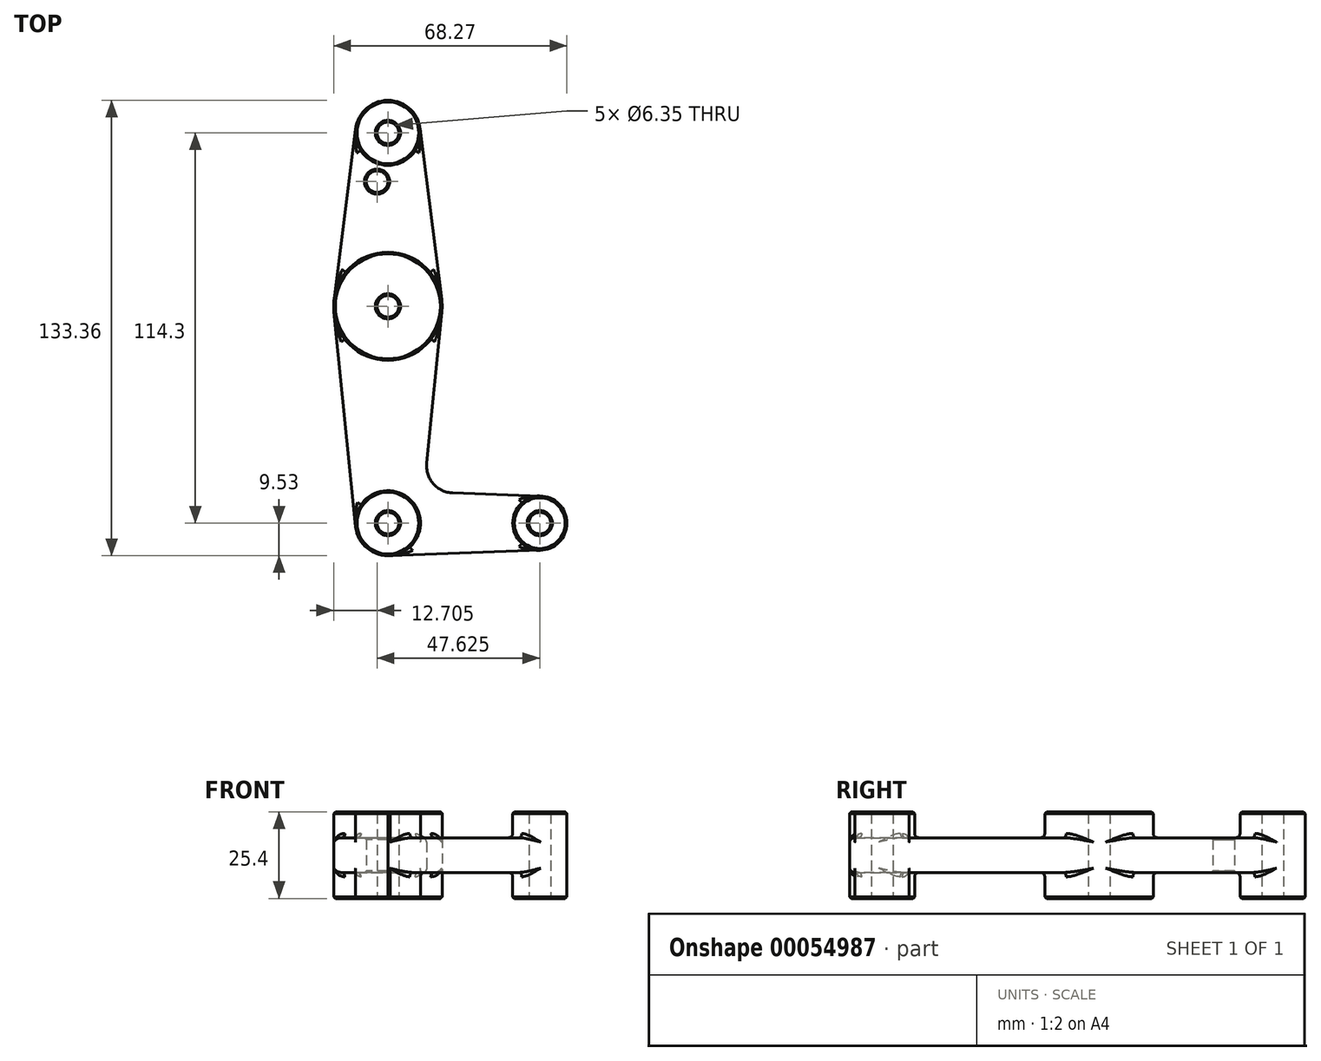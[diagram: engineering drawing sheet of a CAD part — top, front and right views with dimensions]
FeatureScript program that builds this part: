
annotation { "Feature Type Name" : "Feature", "Feature Type Description" : "" }
export const myFeature = defineFeature(function(context is Context, id is Id, definition is map)
    precondition{}
    {
        {
            var Q0;
            Q0=qCreatedBy(makeId("Top.planeOp"),FACE);
            var sketch = newSketch(context, id + "F0", { "sketchPlane" : qUnion([Q0])});
            skCircle(sketch, "E0", {"center": v(0, 0) * mm, "radius": 3.18 * mm});
            skCircle(sketch, "E1", {"center": v(0, 50.8) * mm, "radius": 3.18 * mm});
            skCircle(sketch, "E2", {"center": v(0, -63.5) * mm, "radius": 3.18 * mm});
            skCircle(sketch, "E3", {"center": v(44.45, -63.5) * mm, "radius": 3.18 * mm});
            skCircle(sketch, "E4", {"center": v(-3.18, 36.53) * mm, "radius": 3.18 * mm});
            skCircle(sketch, "E5", {"center": v(0, 0) * mm, "radius": 15.88 * mm});
            skCircle(sketch, "E6", {"center": v(0, 50.8) * mm, "radius": 9.53 * mm});
            skCircle(sketch, "E7", {"center": v(0, -63.5) * mm, "radius": 9.53 * mm});
            skCircle(sketch, "E8", {"center": v(44.45, -63.5) * mm, "radius": 7.94 * mm});
            skLineSegment(sketch, "E9", {"start": v(-15.75, 1.98) * mm, "end": v(-9.45, 52) * mm});
            skLineSegment(sketch, "E10", {"start": v(15.75, 1.98) * mm, "end": v(9.45, 52) * mm});
            skLineSegment(sketch, "E11", {"start": v(-15.8, -1.59) * mm, "end": v(-9.48, -64.45) * mm});
            skLineSegment(sketch, "E12", {"start": v(15.8, -1.59) * mm, "end": v(11.34, -45.9) * mm});
            skLineSegment(sketch, "E13", {"start": v(0, -73.03) * mm, "end": v(44.73, -71.43) * mm});
            skLineSegment(sketch, "E14", {"start": v(18.97, -54.65) * mm, "end": v(44.73, -55.57) * mm});
            skArc(sketch, "E15.filletArc", {"start": v(11.34, -45.9) * mm, "mid": v(13.26, -51.93) * mm, "end": v(18.97, -54.65) * mm});
            skSolve(sketch);
        }
        {
            var Q0;
            {var subQ0=sQuery(id+"F0.wireOp",EDGE,"E11");Q0=makeQuery(id+"F0.imprint","IMPRINT",FACE,{"disambiguationData":[TD([[makeQuery(id+"F0.imprint","IMPRINT",EDGE,{"derivedFrom":subQ0}),1.0]])]});}
            var Q1;
            Q1=makeQuery(id+"F0.imprint","IMPRINT",FACE,{"disambiguationData":[TD([[makeQuery(id+"F0.imprint","IMPRINT",EDGE,{"derivedFrom":sQuery(id+"F0.wireOp",EDGE,"E4")}),-1.0]])]});
            var Q2;
            Q2=makeQuery(id+"F0.imprint","IMPRINT",FACE,{"disambiguationData":[TD([[makeQuery(id+"F0.imprint","IMPRINT",EDGE,{"derivedFrom":sQuery(id+"F0.wireOp",EDGE,"E0")}),-1.0]])]});
            var Q3;
            Q3=makeQuery(id+"F0.imprint","IMPRINT",FACE,{"disambiguationData":[TD([[makeQuery(id+"F0.imprint","IMPRINT",EDGE,{"derivedFrom":sQuery(id+"F0.wireOp",EDGE,"E1")}),-1.0]])]});
            var Q4;
            Q4=makeQuery(id+"F0.imprint","IMPRINT",FACE,{"disambiguationData":[TD([[makeQuery(id+"F0.imprint","IMPRINT",EDGE,{"derivedFrom":sQuery(id+"F0.wireOp",EDGE,"E2")}),-1.0]])]});
            var Q5;
            Q5=makeQuery(id+"F0.imprint","IMPRINT",FACE,{"disambiguationData":[TD([[makeQuery(id+"F0.imprint","IMPRINT",EDGE,{"derivedFrom":sQuery(id+"F0.wireOp",EDGE,"E3")}),-1.0]])]});
            extrude(context, id + "F1", {"entities" : qUnion([Q0, Q1, Q2, Q3, Q4, Q5]), "depth" : 5.08 * mm});
        }
        {
            var Q0;
            Q0=makeQuery(id+"F0.imprint","IMPRINT",FACE,{"disambiguationData":[TD([[makeQuery(id+"F0.imprint","IMPRINT",EDGE,{"derivedFrom":sQuery(id+"F0.wireOp",EDGE,"E2")}),-1.0]])]});
            var Q1;
            Q1=makeQuery(id+"F0.imprint","IMPRINT",FACE,{"disambiguationData":[TD([[makeQuery(id+"F0.imprint","IMPRINT",EDGE,{"derivedFrom":sQuery(id+"F0.wireOp",EDGE,"E3")}),-1.0]])]});
            var Q2;
            Q2=makeQuery(id+"F0.imprint","IMPRINT",FACE,{"disambiguationData":[TD([[makeQuery(id+"F0.imprint","IMPRINT",EDGE,{"derivedFrom":sQuery(id+"F0.wireOp",EDGE,"E1")}),-1.0]])]});
            var Q3;
            Q3=makeQuery(id+"F0.imprint","IMPRINT",FACE,{"disambiguationData":[TD([[makeQuery(id+"F0.imprint","IMPRINT",EDGE,{"derivedFrom":sQuery(id+"F0.wireOp",EDGE,"E0")}),-1.0]])]});
            extrude(context, id + "F2", {"entities" : qUnion([Q0, Q1, Q2, Q3]), "operationType" : NewBodyOperationType.ADD, "depth" : 12.7 * mm});
        }
        {
            var Q0;
            Q0=makeQuery(id+"F1.opExtrude","CAP_EDGE",EDGE,{"disambiguationData":[OSD([sQuery(id+"F0.wireOp",EDGE,"E13")])],"isStart":false});
            var Q1;
            Q1=makeQuery(id+"F1.opExtrude","CAP_EDGE",EDGE,{"disambiguationData":[OSD([sQuery(id+"F0.wireOp",EDGE,"E12")])],"isStart":false});
            var Q2;
            Q2=makeQuery(id+"F1.opExtrude","CAP_EDGE",EDGE,{"disambiguationData":[OSD([sQuery(id+"F0.wireOp",EDGE,"E11")])],"isStart":false});
            var Q3;
            Q3=makeQuery(id+"F1.opExtrude","CAP_EDGE",EDGE,{"disambiguationData":[OSD([sQuery(id+"F0.wireOp",EDGE,"E9")])],"isStart":false});
            var Q4;
            Q4=makeQuery(id+"F1.opExtrude","CAP_EDGE",EDGE,{"disambiguationData":[OSD([sQuery(id+"F0.wireOp",EDGE,"E10")])],"isStart":false});
            fillet(context, id + "F3", {"entities" : qUnion([Q0, Q1, Q2, Q3, Q4]), "radius" : 1.27 * mm, "tangentPropagation" : true, "allowEdgeOverflow" : false});
        }
        {
            var Q0;
            Q0=makeQuery(id+"F2.opExtrude","CAP_EDGE",EDGE,{"disambiguationData":[OSD([sQuery(id+"F0.wireOp",EDGE,"E8")])],"isStart":false});
            var Q1;
            Q1=makeQuery(id+"F2.opExtrude","CAP_EDGE",EDGE,{"disambiguationData":[OSD([sQuery(id+"F0.wireOp",EDGE,"E7")])],"isStart":false});
            var Q2;
            Q2=makeQuery(id+"F2.opExtrude","CAP_EDGE",EDGE,{"disambiguationData":[OSD([sQuery(id+"F0.wireOp",EDGE,"E5")])],"isStart":false});
            var Q3;
            Q3=makeQuery(id+"F2.opExtrude","CAP_EDGE",EDGE,{"disambiguationData":[OSD([sQuery(id+"F0.wireOp",EDGE,"E6")])],"isStart":false});
            var Q4;
            Q4=makeQuery(id+"F1.opExtrude","CAP_EDGE",EDGE,{"disambiguationData":[OSD([sQuery(id+"F0.wireOp",EDGE,"E4")])],"isStart":false});
            var Q5;
            Q5=makeQuery(id+"F2.opExtrude","CAP_EDGE",EDGE,{"disambiguationData":[OSD([sQuery(id+"F0.wireOp",EDGE,"E1")])],"isStart":false});
            var Q6;
            Q6=makeQuery(id+"F2.opExtrude","CAP_FACE",FACE,{"disambiguationData":[OSD([sQuery(id+"F0.wireOp",EDGE,"E0"),sQuery(id+"F0.wireOp",EDGE,"E5")])],"isStart":false});
            var Q7;
            Q7=makeQuery(id+"F2.opExtrude","CAP_EDGE",EDGE,{"disambiguationData":[OSD([sQuery(id+"F0.wireOp",EDGE,"E2")])],"isStart":false});
            var Q8;
            Q8=makeQuery(id+"F2.opExtrude","CAP_EDGE",EDGE,{"disambiguationData":[OSD([sQuery(id+"F0.wireOp",EDGE,"E3")])],"isStart":false});
            chamfer(context, id + "F4", {"entities" : qUnion([Q0, Q1, Q2, Q3, Q4, Q5, Q6, Q7, Q8]), "width" : 0.5 * mm, "tangentPropagation" : true});
        }
        {
            var Q0;
            {var subQ0=sQuery(id+"F0.wireOp",EDGE,"E7");Q0=makeQuery(id+"F2.boolean.opBoolean","INTERSECT",EDGE,{"derivedFrom":[makeQuery(id+"F1.opExtrude","CAP_FACE",FACE,{"disambiguationData":[OSD([sQuery(id+"F0.wireOp",EDGE,"E0"),sQuery(id+"F0.wireOp",EDGE,"E1"),sQuery(id+"F0.wireOp",EDGE,"E2"),sQuery(id+"F0.wireOp",EDGE,"E3"),sQuery(id+"F0.wireOp",EDGE,"E4"),sQuery(id+"F0.wireOp",EDGE,"E5"),sQuery(id+"F0.wireOp",EDGE,"E6"),subQ0,sQuery(id+"F0.wireOp",EDGE,"E8"),sQuery(id+"F0.wireOp",EDGE,"E9"),sQuery(id+"F0.wireOp",EDGE,"E10"),sQuery(id+"F0.wireOp",EDGE,"E11"),sQuery(id+"F0.wireOp",EDGE,"E12"),sQuery(id+"F0.wireOp",EDGE,"E13"),sQuery(id+"F0.wireOp",EDGE,"E14"),sQuery(id+"F0.wireOp",EDGE,"E15.filletArc")])],"isStart":false}),makeQuery(id+"F2.opExtrude","SWEPT_FACE",FACE,{"disambiguationData":[OSD([subQ0])]})]});}
            var Q1;
            {var subQ0=sQuery(id+"F0.wireOp",EDGE,"E5");Q1=makeQuery(id+"F2.boolean.opBoolean","INTERSECT",EDGE,{"disambiguationData":[OD(1.0)],"derivedFrom":[makeQuery(id+"F1.opExtrude","CAP_FACE",FACE,{"disambiguationData":[OSD([sQuery(id+"F0.wireOp",EDGE,"E0"),sQuery(id+"F0.wireOp",EDGE,"E1"),sQuery(id+"F0.wireOp",EDGE,"E2"),sQuery(id+"F0.wireOp",EDGE,"E3"),sQuery(id+"F0.wireOp",EDGE,"E4"),subQ0,sQuery(id+"F0.wireOp",EDGE,"E6"),sQuery(id+"F0.wireOp",EDGE,"E7"),sQuery(id+"F0.wireOp",EDGE,"E8"),sQuery(id+"F0.wireOp",EDGE,"E9"),sQuery(id+"F0.wireOp",EDGE,"E10"),sQuery(id+"F0.wireOp",EDGE,"E11"),sQuery(id+"F0.wireOp",EDGE,"E12"),sQuery(id+"F0.wireOp",EDGE,"E13"),sQuery(id+"F0.wireOp",EDGE,"E14"),sQuery(id+"F0.wireOp",EDGE,"E15.filletArc")])],"isStart":false}),makeQuery(id+"F2.opExtrude","SWEPT_FACE",FACE,{"disambiguationData":[OSD([subQ0])]})]});}
            var Q2;
            {var subQ0=sQuery(id+"F0.wireOp",EDGE,"E5");Q2=makeQuery(id+"F2.boolean.opBoolean","INTERSECT",EDGE,{"disambiguationData":[OD(0.0)],"derivedFrom":[makeQuery(id+"F1.opExtrude","CAP_FACE",FACE,{"disambiguationData":[OSD([sQuery(id+"F0.wireOp",EDGE,"E0"),sQuery(id+"F0.wireOp",EDGE,"E1"),sQuery(id+"F0.wireOp",EDGE,"E2"),sQuery(id+"F0.wireOp",EDGE,"E3"),sQuery(id+"F0.wireOp",EDGE,"E4"),subQ0,sQuery(id+"F0.wireOp",EDGE,"E6"),sQuery(id+"F0.wireOp",EDGE,"E7"),sQuery(id+"F0.wireOp",EDGE,"E8"),sQuery(id+"F0.wireOp",EDGE,"E9"),sQuery(id+"F0.wireOp",EDGE,"E10"),sQuery(id+"F0.wireOp",EDGE,"E11"),sQuery(id+"F0.wireOp",EDGE,"E12"),sQuery(id+"F0.wireOp",EDGE,"E13"),sQuery(id+"F0.wireOp",EDGE,"E14"),sQuery(id+"F0.wireOp",EDGE,"E15.filletArc")])],"isStart":false}),makeQuery(id+"F2.opExtrude","SWEPT_FACE",FACE,{"disambiguationData":[OSD([subQ0])]})]});}
            var Q3;
            {var subQ0=sQuery(id+"F0.wireOp",EDGE,"E6");Q3=makeQuery(id+"F2.boolean.opBoolean","INTERSECT",EDGE,{"derivedFrom":[makeQuery(id+"F1.opExtrude","CAP_FACE",FACE,{"disambiguationData":[OSD([sQuery(id+"F0.wireOp",EDGE,"E0"),sQuery(id+"F0.wireOp",EDGE,"E1"),sQuery(id+"F0.wireOp",EDGE,"E2"),sQuery(id+"F0.wireOp",EDGE,"E3"),sQuery(id+"F0.wireOp",EDGE,"E4"),sQuery(id+"F0.wireOp",EDGE,"E5"),subQ0,sQuery(id+"F0.wireOp",EDGE,"E7"),sQuery(id+"F0.wireOp",EDGE,"E8"),sQuery(id+"F0.wireOp",EDGE,"E9"),sQuery(id+"F0.wireOp",EDGE,"E10"),sQuery(id+"F0.wireOp",EDGE,"E11"),sQuery(id+"F0.wireOp",EDGE,"E12"),sQuery(id+"F0.wireOp",EDGE,"E13"),sQuery(id+"F0.wireOp",EDGE,"E14"),sQuery(id+"F0.wireOp",EDGE,"E15.filletArc")])],"isStart":false}),makeQuery(id+"F2.opExtrude","SWEPT_FACE",FACE,{"disambiguationData":[OSD([subQ0])]})]});}
            var Q4;
            {var subQ0=sQuery(id+"F0.wireOp",EDGE,"E8");Q4=makeQuery(id+"F2.boolean.opBoolean","INTERSECT",EDGE,{"derivedFrom":[makeQuery(id+"F1.opExtrude","CAP_FACE",FACE,{"disambiguationData":[OSD([sQuery(id+"F0.wireOp",EDGE,"E0"),sQuery(id+"F0.wireOp",EDGE,"E1"),sQuery(id+"F0.wireOp",EDGE,"E2"),sQuery(id+"F0.wireOp",EDGE,"E3"),sQuery(id+"F0.wireOp",EDGE,"E4"),sQuery(id+"F0.wireOp",EDGE,"E5"),sQuery(id+"F0.wireOp",EDGE,"E6"),sQuery(id+"F0.wireOp",EDGE,"E7"),subQ0,sQuery(id+"F0.wireOp",EDGE,"E9"),sQuery(id+"F0.wireOp",EDGE,"E10"),sQuery(id+"F0.wireOp",EDGE,"E11"),sQuery(id+"F0.wireOp",EDGE,"E12"),sQuery(id+"F0.wireOp",EDGE,"E13"),sQuery(id+"F0.wireOp",EDGE,"E14"),sQuery(id+"F0.wireOp",EDGE,"E15.filletArc")])],"isStart":false}),makeQuery(id+"F2.opExtrude","SWEPT_FACE",FACE,{"disambiguationData":[OSD([subQ0])]})]});}
            fillet(context, id + "F5", {"entities" : qUnion([Q0, Q1, Q2, Q3, Q4]), "radius" : 1.27 * mm, "tangentPropagation" : true, "allowEdgeOverflow" : false});
        }
        {
            var Q0;
            Q0=makeQuery(id+"F1.opExtrude","SWEPT_BODY",BODY,{"disambiguationData":[OSD([sQuery(id+"F0.wireOp",EDGE,"E0"),sQuery(id+"F0.wireOp",EDGE,"E1"),sQuery(id+"F0.wireOp",EDGE,"E2"),sQuery(id+"F0.wireOp",EDGE,"E3"),sQuery(id+"F0.wireOp",EDGE,"E4"),sQuery(id+"F0.wireOp",EDGE,"E5"),sQuery(id+"F0.wireOp",EDGE,"E6"),sQuery(id+"F0.wireOp",EDGE,"E7"),sQuery(id+"F0.wireOp",EDGE,"E8"),sQuery(id+"F0.wireOp",EDGE,"E9"),sQuery(id+"F0.wireOp",EDGE,"E10"),sQuery(id+"F0.wireOp",EDGE,"E11"),sQuery(id+"F0.wireOp",EDGE,"E12"),sQuery(id+"F0.wireOp",EDGE,"E13"),sQuery(id+"F0.wireOp",EDGE,"E14"),sQuery(id+"F0.wireOp",EDGE,"E15.filletArc")])]});
            var Q1;
            Q1=qCreatedBy(makeId("Top.planeOp"),FACE);
            mirror(context, id + "F6", {"operationType" : NewBodyOperationType.ADD, "entities" : qUnion([Q0]), "mirrorPlane" : qUnion([Q1])});
        }
    });
